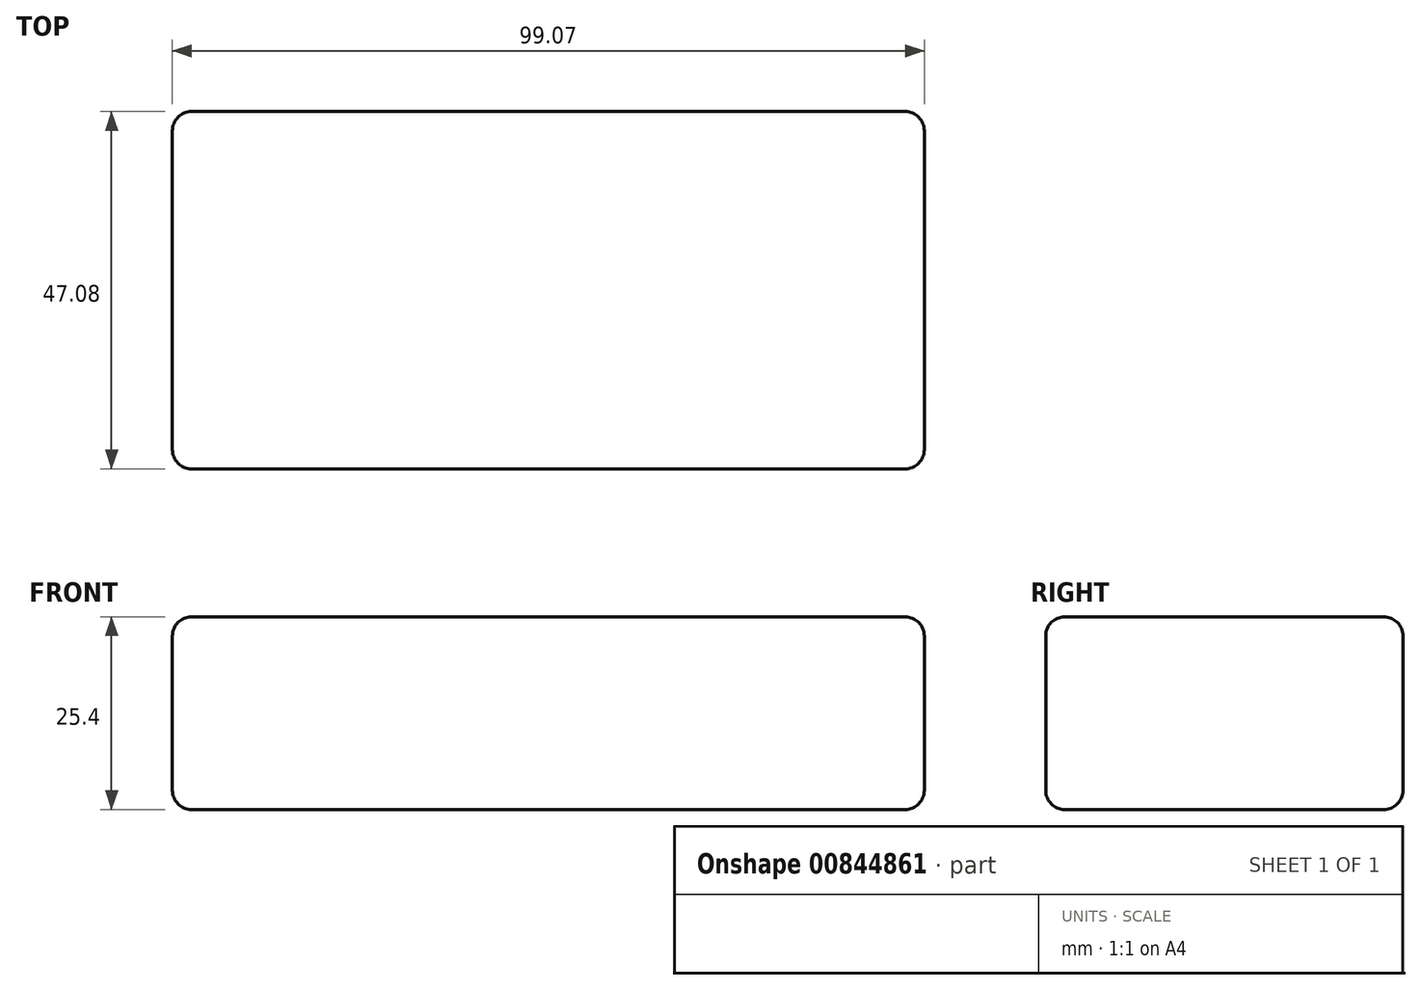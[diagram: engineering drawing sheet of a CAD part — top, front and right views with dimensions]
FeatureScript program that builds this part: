
annotation { "Feature Type Name" : "Feature", "Feature Type Description" : "" }
export const myFeature = defineFeature(function(context is Context, id is Id, definition is map)
    precondition{}
    {
        {
            var Q0;
            Q0=qCreatedBy(makeId("Top.planeOp"),FACE);
            var sketch = newSketch(context, id + "F0", { "sketchPlane" : qUnion([Q0])});
            skLineSegment(sketch, "E0.bottom", {"start": v(-48.81, 21.52) * mm, "end": v(50.26, 21.52) * mm});
            skLineSegment(sketch, "E0.top", {"start": v(-48.81, -25.56) * mm, "end": v(50.26, -25.56) * mm});
            skLineSegment(sketch, "E0.left", {"start": v(-48.81, 21.52) * mm, "end": v(-48.81, -25.56) * mm});
            skLineSegment(sketch, "E0.right", {"start": v(50.26, 21.52) * mm, "end": v(50.26, -25.56) * mm});
            skSolve(sketch);
        }
        {
            var Q0;
            Q0 = qSketchRegion(id + "F0", true);
            extrude(context, id + "F1", {"entities" : qUnion([Q0]), "depth" : 25.4 * mm, "offsetDistance" : 25.4 * mm});
        }
        {
            var Q0;
            Q0=makeQuery(id+"F1.opExtrude","CAP_EDGE",EDGE,{"disambiguationData":[OSD([sQuery(id+"F0.wireOp",EDGE,"E0.left")])],"isStart":true});
            var Q1;
            Q1=makeQuery(id+"F1.opExtrude","CAP_EDGE",EDGE,{"disambiguationData":[OSD([sQuery(id+"F0.wireOp",EDGE,"E0.top")])],"isStart":true});
            var Q2;
            Q2=makeQuery(id+"F1.opExtrude","CAP_EDGE",EDGE,{"disambiguationData":[OSD([sQuery(id+"F0.wireOp",EDGE,"E0.bottom")])],"isStart":true});
            var Q3;
            Q3=makeQuery(id+"F1.opExtrude","CAP_EDGE",EDGE,{"disambiguationData":[OSD([sQuery(id+"F0.wireOp",EDGE,"E0.right")])],"isStart":true});
            var Q4;
            Q4=makeQuery(id+"F1.opExtrude","CAP_EDGE",EDGE,{"disambiguationData":[OSD([sQuery(id+"F0.wireOp",EDGE,"E0.top")])],"isStart":false});
            var Q5;
            Q5=makeQuery(id+"F1.opExtrude","SWEPT_EDGE",EDGE,{"disambiguationData":[OSD([sQuery(id+"F0.wireOp",EDGE,"E0.top"),sQuery(id+"F0.wireOp",EDGE,"E0.left")])]});
            var Q6;
            Q6=makeQuery(id+"F1.opExtrude","SWEPT_EDGE",EDGE,{"disambiguationData":[OSD([sQuery(id+"F0.wireOp",EDGE,"E0.top"),sQuery(id+"F0.wireOp",EDGE,"E0.right")])]});
            var Q7;
            Q7=makeQuery(id+"F1.opExtrude","CAP_FACE",FACE,{"disambiguationData":[OSD([sQuery(id+"F0.wireOp",EDGE,"E0.bottom"),sQuery(id+"F0.wireOp",EDGE,"E0.top"),sQuery(id+"F0.wireOp",EDGE,"E0.left"),sQuery(id+"F0.wireOp",EDGE,"E0.right")])],"isStart":false});
            var Q8;
            Q8=makeQuery(id+"F1.opExtrude","SWEPT_EDGE",EDGE,{"disambiguationData":[OSD([sQuery(id+"F0.wireOp",EDGE,"E0.bottom"),sQuery(id+"F0.wireOp",EDGE,"E0.right")])]});
            var Q9;
            Q9=makeQuery(id+"F1.opExtrude","SWEPT_EDGE",EDGE,{"disambiguationData":[OSD([sQuery(id+"F0.wireOp",EDGE,"E0.bottom"),sQuery(id+"F0.wireOp",EDGE,"E0.left")])]});
            fillet(context, id + "F2", {"entities" : qUnion([Q0, Q1, Q2, Q3, Q4, Q5, Q6, Q7, Q8, Q9]), "radius" : 2.54 * mm, "tangentPropagation" : true, "allowEdgeOverflow" : false});
        }
    });
